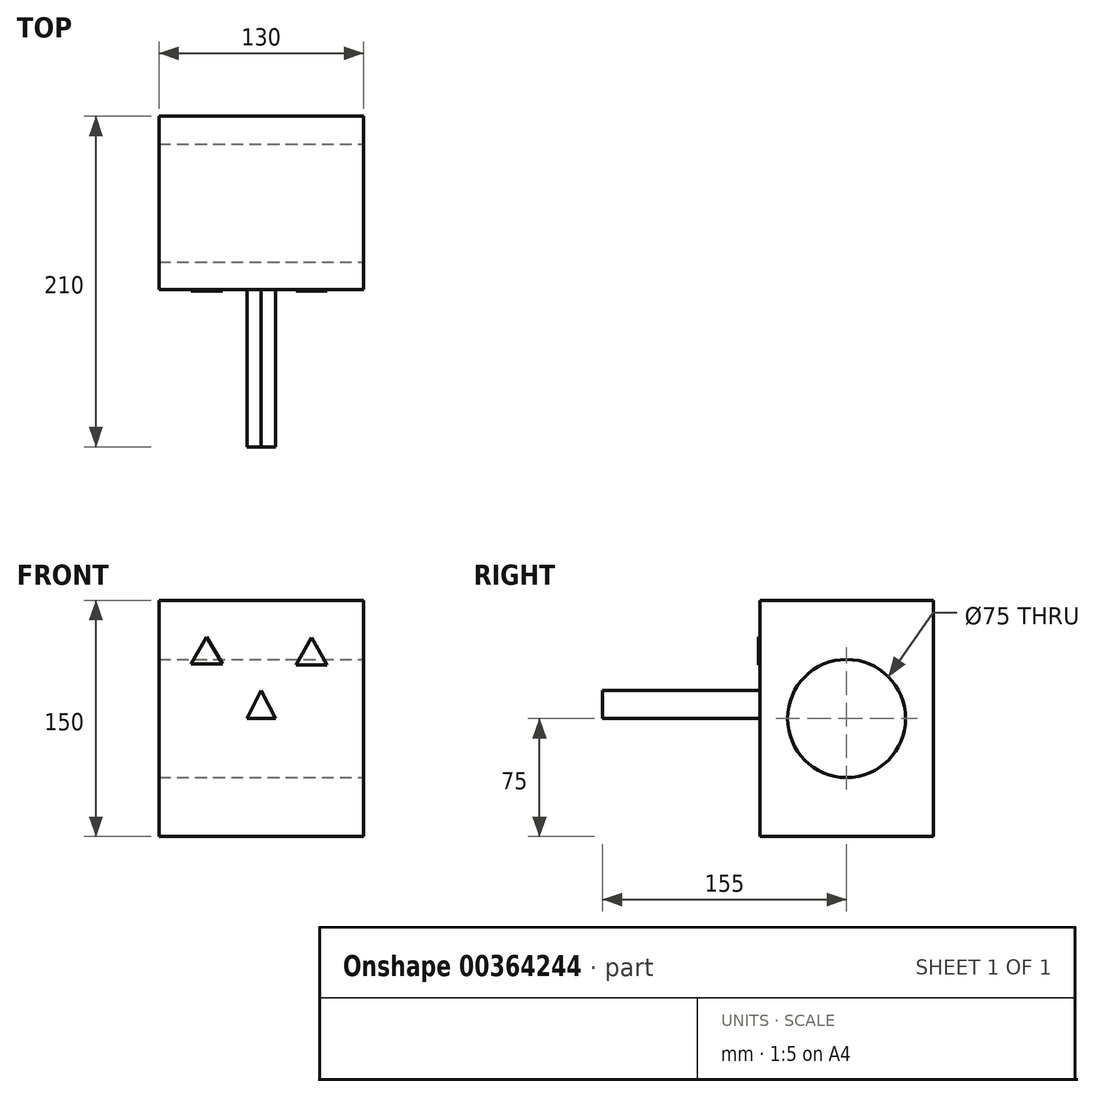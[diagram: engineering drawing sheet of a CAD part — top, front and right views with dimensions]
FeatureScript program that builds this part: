
annotation { "Feature Type Name" : "Feature", "Feature Type Description" : "" }
export const myFeature = defineFeature(function(context is Context, id is Id, definition is map)
    precondition{}
    {
        {
            var Q0;
            Q0=qCreatedBy(makeId("Front.planeOp"),FACE);
            var sketch = newSketch(context, id + "F0", { "sketchPlane" : qUnion([Q0])});
            skLineSegment(sketch, "E0.bottom", {"start": v(65, 75) * mm, "end": v(-65, 75) * mm});
            skLineSegment(sketch, "E0.top", {"start": v(65, -75) * mm, "end": v(-65, -75) * mm});
            skLineSegment(sketch, "E0.left", {"start": v(65, 75) * mm, "end": v(65, -75) * mm});
            skLineSegment(sketch, "E0.right", {"start": v(-65, 75) * mm, "end": v(-65, -75) * mm});
            skPoint(sketch, "E0.middle", {"position": v(0, 0) * mm});
            skSolve(sketch);
        }
        {
            var Q0;
            Q0 = qSketchRegion(id + "F0", true);
            extrude(context, id + "F1", {"entities" : qUnion([Q0]), "oppositeDirection" : true, "depth" : 110 * mm});
        }
        {
            var Q0;
            Q0=makeQuery(id+"F1.opExtrude","SWEPT_FACE",FACE,{"disambiguationData":[OSD([sQuery(id+"F0.wireOp",EDGE,"E0.left")])]});
            var sketch = newSketch(context, id + "F2", { "sketchPlane" : qUnion([Q0])});
            skCircle(sketch, "E1", {"center": v(55, 0) * mm, "radius": 37.5 * mm});
            skPoint(sketch, "E1.centerSnap0", {"position": v(55, 75) * mm});
            skSolve(sketch);
        }
        {
            var Q0;
            Q0=makeQuery(id+"F2.imprint","IMPRINT",FACE,{"disambiguationData":[TD([[makeQuery(id+"F2.imprint","IMPRINT",EDGE,{"derivedFrom":sQuery(id+"F2.wireOp",EDGE,"E1")}),1.0]])]});
            extrude(context, id + "F3", {"entities" : qUnion([Q0]), "operationType" : NewBodyOperationType.REMOVE, "oppositeDirection" : true, "depth" : 130 * mm});
        }
        {
            var Q0;
            Q0=qCreatedBy(makeId("Front.planeOp"),FACE);
            var sketch = newSketch(context, id + "F4", { "sketchPlane" : qUnion([Q0])});
            skLineSegment(sketch, "E2.0", {"start": v(-24.62, 34.5) * mm, "end": v(-44.62, 34.55) * mm});
            skLineSegment(sketch, "E2.1", {"start": v(-44.62, 34.55) * mm, "end": v(-34.59, 51.85) * mm});
            skLineSegment(sketch, "E2.2", {"start": v(-34.59, 51.85) * mm, "end": v(-24.62, 34.5) * mm});
            skLineSegment(sketch, "E3.0", {"start": v(9, 0) * mm, "end": v(-9, 0) * mm});
            skLineSegment(sketch, "E3.1", {"start": v(-9, 0) * mm, "end": v(0, 17.86) * mm});
            skLineSegment(sketch, "E3.2", {"start": v(0, 17.86) * mm, "end": v(9, 0) * mm});
            skLineSegment(sketch, "E4.0", {"start": v(41.96, 34.15) * mm, "end": v(21.96, 34.18) * mm});
            skLineSegment(sketch, "E4.1", {"start": v(21.96, 34.18) * mm, "end": v(32, 51.49) * mm});
            skLineSegment(sketch, "E4.2", {"start": v(32, 51.49) * mm, "end": v(41.96, 34.15) * mm});
            skLineSegment(sketch, "E5", {"start": v(-38.08, -37.97) * mm, "end": v(38.76, -37.97) * mm});
            skSolve(sketch);
        }
        {
            var Q0;
            Q0=makeQuery(id+"F4.imprint","IMPRINT",FACE,{"disambiguationData":[TD([[makeQuery(id+"F4.imprint","IMPRINT",EDGE,{"derivedFrom":sQuery(id+"F4.wireOp",EDGE,"E3.0")}),-1.0]])]});
            extrude(context, id + "F5", {"entities" : qUnion([Q0]), "operationType" : NewBodyOperationType.ADD, "depth" : 100 * mm});
        }
        {
            var Q0;
            Q0=makeQuery(id+"F4.imprint","IMPRINT",FACE,{"disambiguationData":[TD([[makeQuery(id+"F4.imprint","IMPRINT",EDGE,{"derivedFrom":sQuery(id+"F4.wireOp",EDGE,"E2.0")}),-1.0]])]});
            var Q1;
            Q1=makeQuery(id+"F4.imprint","IMPRINT",FACE,{"disambiguationData":[TD([[makeQuery(id+"F4.imprint","IMPRINT",EDGE,{"derivedFrom":sQuery(id+"F4.wireOp",EDGE,"E4.0")}),-1.0]])]});
            extrude(context, id + "F6", {"entities" : qUnion([Q0, Q1]), "operationType" : NewBodyOperationType.ADD, "depth" : 1 * mm});
        }
    });
